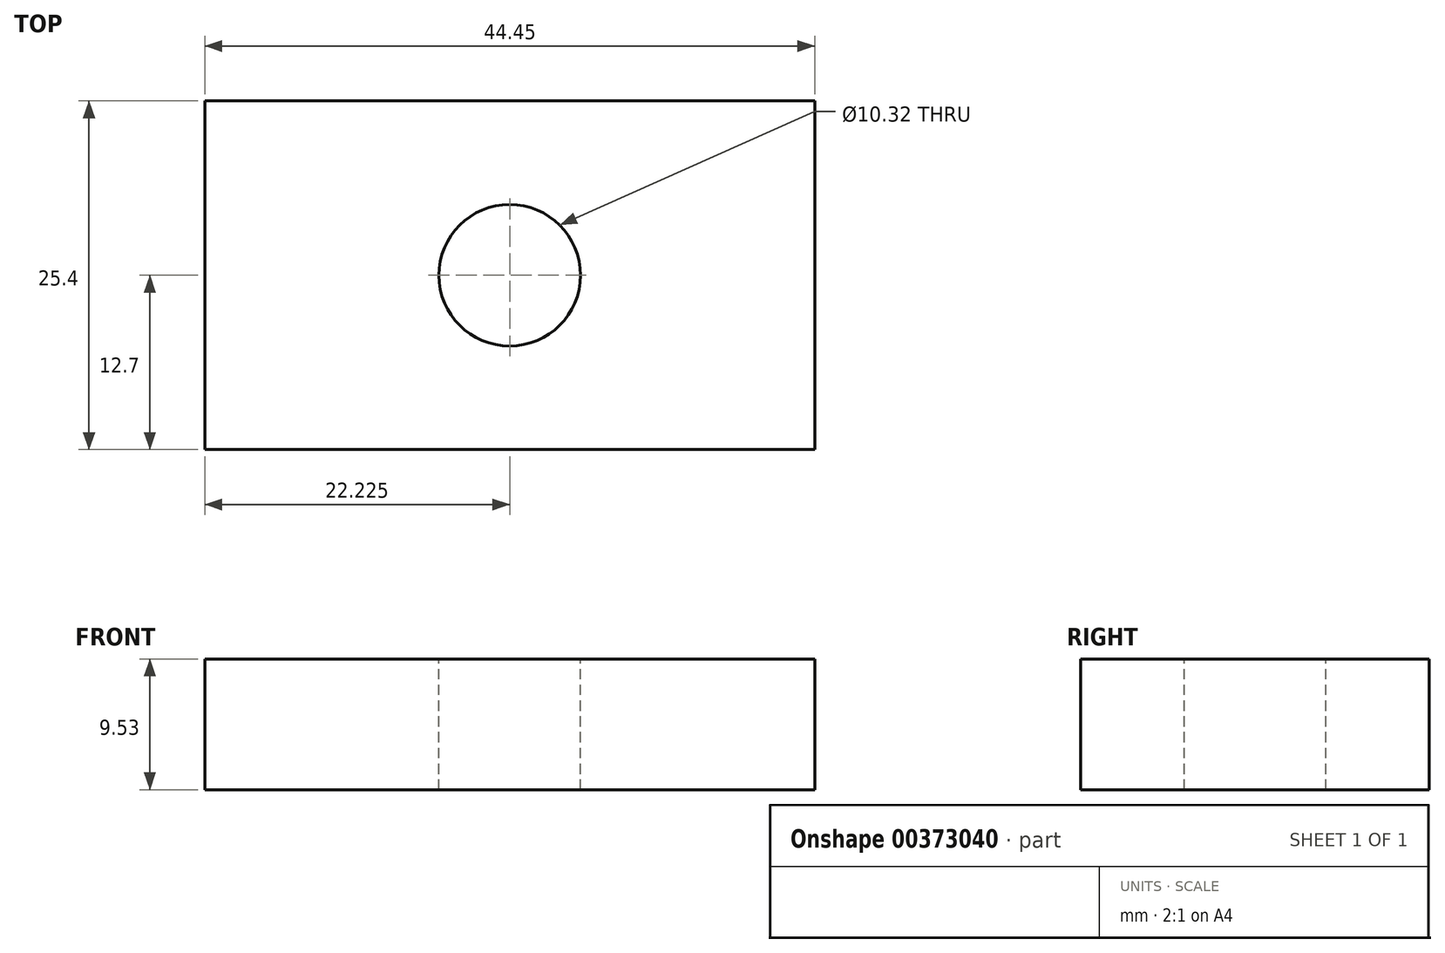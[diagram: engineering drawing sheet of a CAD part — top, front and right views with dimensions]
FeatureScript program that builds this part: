
annotation { "Feature Type Name" : "Feature", "Feature Type Description" : "" }
export const myFeature = defineFeature(function(context is Context, id is Id, definition is map)
    precondition{}
    {
        {
            var Q0;
            Q0=qCreatedBy(makeId("Top.planeOp"),FACE);
            var sketch = newSketch(context, id + "F0", { "sketchPlane" : qUnion([Q0])});
            skLineSegment(sketch, "E0.bottom", {"start": v(0, 0) * mm, "end": v(-44.45, 0) * mm});
            skLineSegment(sketch, "E0.top", {"start": v(0, 25.4) * mm, "end": v(-44.45, 25.4) * mm});
            skLineSegment(sketch, "E0.left", {"start": v(0, 0) * mm, "end": v(0, 25.4) * mm});
            skLineSegment(sketch, "E0.right", {"start": v(-44.45, 0) * mm, "end": v(-44.45, 25.4) * mm});
            skSolve(sketch);
        }
        {
            var Q0;
            Q0=makeQuery(id+"F0.imprint","IMPRINT",FACE,{"disambiguationData":[TD([[makeQuery(id+"F0.imprint","IMPRINT",EDGE,{"derivedFrom":sQuery(id+"F0.wireOp",EDGE,"E0.bottom")}),-1.0]])]});
            extrude(context, id + "F1", {"entities" : qUnion([Q0]), "depth" : 9.52 * mm});
        }
        {
            var Q0;
            Q0=makeQuery(id+"F1.opExtrude","CAP_FACE",FACE,{"disambiguationData":[OSD([sQuery(id+"F0.wireOp",EDGE,"E0.bottom"),sQuery(id+"F0.wireOp",EDGE,"E0.top"),sQuery(id+"F0.wireOp",EDGE,"E0.left"),sQuery(id+"F0.wireOp",EDGE,"E0.right")])],"isStart":false});
            var sketch = newSketch(context, id + "F2", { "sketchPlane" : qUnion([Q0])});
            skLineSegment(sketch, "E1", {"start": v(-44.45, 12.7) * mm, "end": v(-22.23, 12.7) * mm});
            skPoint(sketch, "E1.endSnap0", {"position": v(-22.23, 0) * mm});
            skPoint(sketch, "E2", {"position": v(-22.23, 12.7) * mm});
            skSolve(sketch);
        }
        {
            var Q0;
            Q0=sQuery(id+"F2.wireOp",VERTEX,"E2");
            var Q1;
            Q1=makeQuery(id+"F1.opExtrude","SWEPT_BODY",BODY,{"disambiguationData":[OSD([sQuery(id+"F0.wireOp",EDGE,"E0.bottom"),sQuery(id+"F0.wireOp",EDGE,"E0.top"),sQuery(id+"F0.wireOp",EDGE,"E0.left"),sQuery(id+"F0.wireOp",EDGE,"E0.right")])]});
            hole(context, id + "F3", {"style" : HoleStyle.SIMPLE, "endStyle" : HoleEndStyle.THROUGH, "holeDiameter" : 10.32 * mm, "isTappedThrough" : true, "tappedDepth" : 12.7 * mm, "tapClearance" : 3, "startFromSketch" : true, "locations" : qUnion([Q0]), "scope" : qUnion([Q1])});
        }
    });
